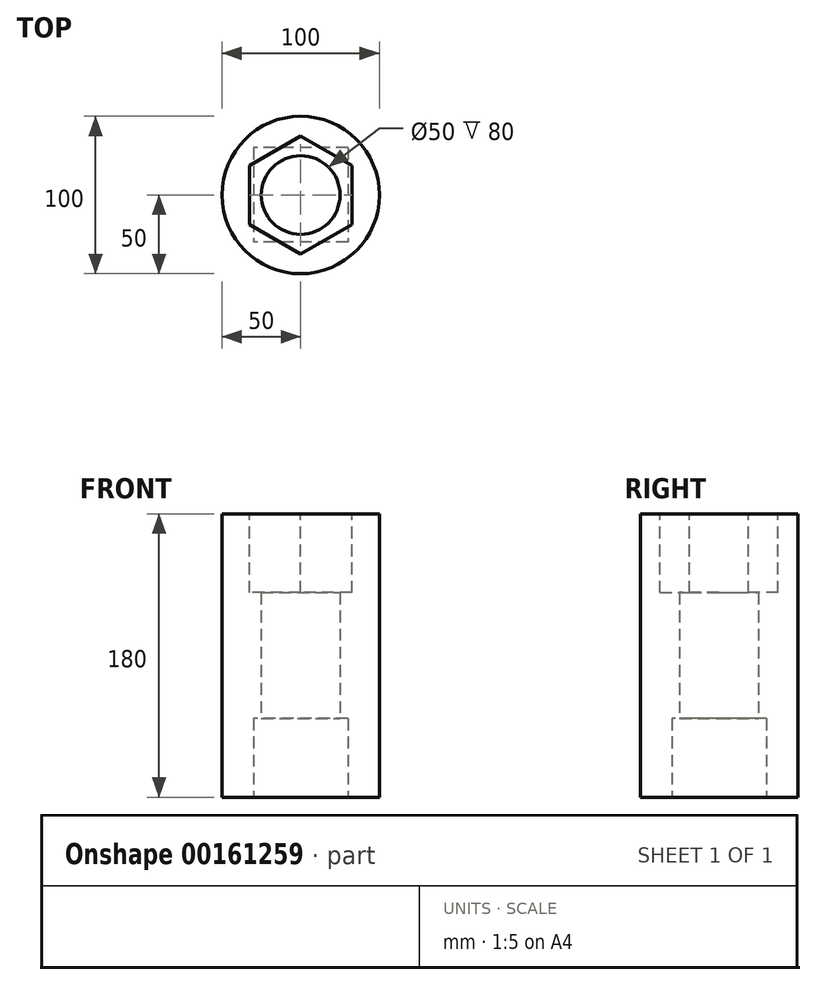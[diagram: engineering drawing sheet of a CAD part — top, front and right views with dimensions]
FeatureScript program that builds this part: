
annotation { "Feature Type Name" : "Feature", "Feature Type Description" : "" }
export const myFeature = defineFeature(function(context is Context, id is Id, definition is map)
    precondition{}
    {
        {
            var Q0;
            Q0=qCreatedBy(makeId("Top.planeOp"),FACE);
            var sketch = newSketch(context, id + "F0", { "sketchPlane" : qUnion([Q0])});
            skCircle(sketch, "E0", {"center": v(0, 0) * mm, "radius": 50 * mm});
            skSolve(sketch);
        }
        {
            var Q0;
            Q0 = qSketchRegion(id + "F0", true);
            extrude(context, id + "F1", {"entities" : qUnion([Q0]), "depth" : 180 * mm});
        }
        {
            var Q0;
            Q0=qCreatedBy(makeId("Top.planeOp"),FACE);
            var sketch = newSketch(context, id + "F2", { "sketchPlane" : qUnion([Q0])});
            skCircle(sketch, "E1", {"center": v(0, 0) * mm, "radius": 25 * mm});
            skSolve(sketch);
        }
        {
            var Q0;
            Q0 = qSketchRegion(id + "F2", true);
            extrude(context, id + "F3", {"entities" : qUnion([Q0]), "operationType" : NewBodyOperationType.REMOVE, "endBound" : BoundingType.UP_TO_NEXT, "depth" : 25 * mm});
        }
        {
            var Q0;
            Q0=makeQuery(id+"F1.opExtrude","CAP_FACE",FACE,{"disambiguationData":[OSD([sQuery(id+"F0.wireOp",EDGE,"E0")])],"isStart":false});
            var sketch = newSketch(context, id + "F4", { "sketchPlane" : qUnion([Q0])});
            skCircle(sketch, "E2.cCircle", {"center": v(0, 0) * mm, "radius": 32.5 * mm, "construction": true});
            skLineSegment(sketch, "E2.0", {"start": v(-32.5, -18.76) * mm, "end": v(-32.5, 18.76) * mm});
            skLineSegment(sketch, "E2.1", {"start": v(-32.5, 18.76) * mm, "end": v(0, 37.53) * mm});
            skLineSegment(sketch, "E2.2", {"start": v(0, 37.53) * mm, "end": v(32.5, 18.76) * mm});
            skLineSegment(sketch, "E2.3", {"start": v(32.5, 18.76) * mm, "end": v(32.5, -18.76) * mm});
            skLineSegment(sketch, "E2.4", {"start": v(32.5, -18.76) * mm, "end": v(0, -37.53) * mm});
            skLineSegment(sketch, "E2.5", {"start": v(0, -37.53) * mm, "end": v(-32.5, -18.76) * mm});
            skPoint(sketch, "E2.0.midPoint", {"position": v(-32.5, 0) * mm});
            skSolve(sketch);
        }
        {
            var Q0;
            Q0 = qSketchRegion(id + "F4", true);
            extrude(context, id + "F5", {"entities" : qUnion([Q0]), "operationType" : NewBodyOperationType.REMOVE, "oppositeDirection" : true, "depth" : 50 * mm});
        }
        {
            var Q0;
            Q0=makeQuery(id+"F1.opExtrude","CAP_FACE",FACE,{"disambiguationData":[OSD([sQuery(id+"F0.wireOp",EDGE,"E0")])],"isStart":true});
            var sketch = newSketch(context, id + "F6", { "sketchPlane" : qUnion([Q0])});
            skLineSegment(sketch, "E3.bottom", {"start": v(30, -30) * mm, "end": v(-30, -30) * mm});
            skLineSegment(sketch, "E3.top", {"start": v(30, 30) * mm, "end": v(-30, 30) * mm});
            skLineSegment(sketch, "E3.left", {"start": v(30, -30) * mm, "end": v(30, 30) * mm});
            skLineSegment(sketch, "E3.right", {"start": v(-30, -30) * mm, "end": v(-30, 30) * mm});
            skPoint(sketch, "E3.middle", {"position": v(0, 0) * mm});
            skSolve(sketch);
        }
        {
            var Q0;
            Q0 = qSketchRegion(id + "F6", true);
            extrude(context, id + "F7", {"entities" : qUnion([Q0]), "operationType" : NewBodyOperationType.REMOVE, "oppositeDirection" : true, "depth" : 50 * mm});
        }
    });
